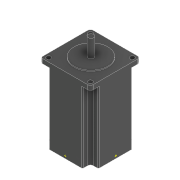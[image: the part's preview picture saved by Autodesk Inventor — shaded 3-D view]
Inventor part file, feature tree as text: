
AUTODESK INVENTOR PART (.ipt)
format: ipt  version: 2022 (Build 260153000, 153)  size: 235,008 bytes
history: native  units: mm
features: sketch x8, extrude x5, projected_geometry x1
ambient origin geometry x8: Origin, YZ Plane, XZ Plane, XY Plane, X Axis, Y Axis, Z Axis, Center Point
bodies: Solid1 (feature_tree)
feature tree (14):
  extrude  "Extrusion1"  Depth=56.2mm
  extrude  "Extrusion2"  Depth=4.5mm
  extrude  "Extrusion3"  Depth=5.0mm
  extrude  "Extrusion4"  Depth=2.0mm
  extrude  "Extrusion5"  Depth=3.0mm
  sketch  "Sketch6"  dims[d10=5.0mm d11=0.0mm]
  sketch  "Sketch7"  dims[d12=38.0mm]
  sketch  "Sketch8"  dims[d13=1.0mm d14=0.0mm d15=6.4mm d16=6.1mm d17=20.0mm d18=0.0mm d19=9.0mm d20=9.0mm d21=3.0mm d22=9.0mm d23=9.0mm d24=3.0mm d25=80.0mm d26=0.0mm d27=1.0mm d28=18.1mm d29=5.0mm d30=12.0mm d31=10.0mm d32=1.0mm d33=0.0mm d34=4.5mm d35=4.5mm d36=3.0mm d37=3.0mm]
  sketch  "Sketch1"  dims[d0=56.2mm d1=56.2mm]
  sketch  "Sketch2"  dims[d2=4.5mm d3=4.5mm]
  sketch  "Sketch3"  dims[d4=5.0mm d5=4.5mm]
  sketch  "Sketch4"  dims[d6=4.5mm d7=2.0mm]
  sketch  "Sketch5"  dims[d8=3.0mm d9=38.0mm]
  projected_geometry  "Projected Loop1"
